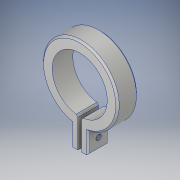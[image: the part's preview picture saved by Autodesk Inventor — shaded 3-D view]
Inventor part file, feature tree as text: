
AUTODESK INVENTOR PART (.ipt)
format: ipt  version: 2019 (Build 230136000, 136)  size: 163,328 bytes
history: native  units: mm
features: sketch x3, hole x2, extrude x1, chamfer x1
ambient origin geometry x8: Origin, YZ Plane, XZ Plane, XY Plane, X Axis, Y Axis, Z Axis, Center Point
bodies: Solide1 (feature_tree)
feature tree (7):
  extrude  "Extrusion1"  Depth=8.0mm
  chamfer  "Chanfrein1"  Distance=1.0mm
  hole  "Perçage1"  [1 undecoded]
  hole  "Perçage2"  [1 undecoded]
  sketch  "Esquisse1"
  sketch  "Esquisse2"
  sketch  "Esquisse3"
note: 2 required parameter values undecoded (feature->parameter linkage not recoverable at this tier; creation-order binding heuristic only, values carry confidence <= 0.55)
